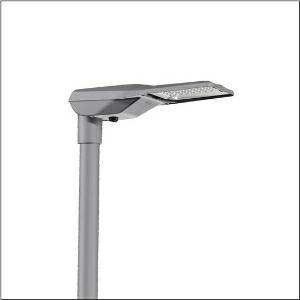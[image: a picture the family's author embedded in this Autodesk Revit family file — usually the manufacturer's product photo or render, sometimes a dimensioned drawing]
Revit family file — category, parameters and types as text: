
# Revit family: streetlight_sl_21_iq_mini___p0_8a_5xe2u31u08jb_01d9
name_source: partatom
category: Lighting Fixtures
units: mm (PartAtom-declared; Revit-internal decimal feet)

## family parameters
Cut with Voids When Loaded = No
Host = Face
Light Source = No
Part Type = Normal
Room Calculation Point = No
Round Connector Dimension = Use Diameter
Shared = No

## types (1)
- --- (1 x LED, 11310 lm, 72.5 W, 3000K)
    Apparent Load = 73 VA
    CIE Flux Codes = 36 69 97 100 100
    Color Rendering = 70
    Color Temperature = 3000K
    Default Elevation = 1800 mm
    Description = Streetlight SL 21 iQ mini, mast luminaire, primary light control with lens, of PMMA, primary optical cover: cover, of toughened safety glass, transparent, light distribution: P0.8a, light emission: direct distribution, primary light characteristic: asymmetric, installation type: post-top, side-entry, LED, High Power LED, rated luminous flux: 11.310lm, luminous efficacy: 156lm/W, light colour: 730, colour temperature: 3000K, control gear: iQ-Street Remote, D4i with power reduction, control: pre-setting: logarithmic dimming characteristic, Street-Remote, Auto-Match, Temp-Guard, Lumen-Switch, Night-Set, Smart-Wire, Light-Fading, Desk-Remote (wireless, voltage-free reading and setting of iQ features in the workshop via application-optimized NFC function/RFID function), optimised constant luminous flux control (CLO 2.0), mains connection: 220..240V, AC, 50/60Hz, start of lifetime: 73W, end of service life: 76W, reduction: 33W, luminaire housing, of diecast aluminium, powder-coated, Siteco® metallic grey (DB 702S), corrosivity category C5 mid according to DIN EN ISO 12944, please order mast flange separately, inclination adjustable: 0°, 5°, 10°, 15°, sealing non-destructively replaceable, multi-level sealing system, length: 628mm, width: 235mm, height: 110mm, mast flange for spigot size: 42mm (side-entry): 5XC10008XM4, 60/48mm (side-entry/post-top): 5XC10108XM2, 76/60mm (side-entry/post-top): 5XC10108XM1, mounting height: 4..8m, Smart Interface below, protection rating (complete): IP66, insulation class (complete): insulation class II (safety insulation), certification: CE, ENEC, ENEC+, VDE, impact resistance: IK10, permissible operating ambient temperature for outdoor applications: -40..+50°C, standard-compliant lighting for roads and squares, packaging unit: 1 piece

Light Distribution: P0.8a
    Height = 110 mm
    Lamp = 1 x LED
    Lamp Light Flux = 11310 lm
    Lamp Power = 72.5 W
    Lamp count = 1
    Length = 625 mm
    Luminous efficacy = 156 lm/W
    Manufacturer = Siteco
    ModVariant = No
    Model = 5XE2U31U08JB
    Number of Poles = 1
    OnlyDefault = Yes
    Power Factor = 1
    Product Name = Streetlight SL 21 iQ mini | P0.8a
    Product group = mast luminaire | pylon top
    ProductGroupID = 6100
    Protection Class = Protection class II
    Protection Degree = IP 66
    RLX_Detail_Level = 1
    RLX_Emergency_Light_Flux = 0 lm
    RLX_Emergency_Type = 0
    RLX_Emergency_Type_DB = No
    RlxData = <blob elided: 26361 chars, md5=41e64e7d>
    Socket = socket
    Standby Power = 0 W
    System Light Flux = 11310 lm
    System Power = 73 W
    Type Comments = factory setting: luminous flux: 100 % | dim-lin: 254 | 755 mA
    Type Image = l_1003516.jpg
    URL = http://relux.com
    VarID = @adj_072174
    Voltage = 0 V
    Weight = 0.00 kg
    Width = 234 mm

## geometry (parser evidence)
native form markers: Blend x4, Sweep x10
no freeform markers — native parametric forms only
